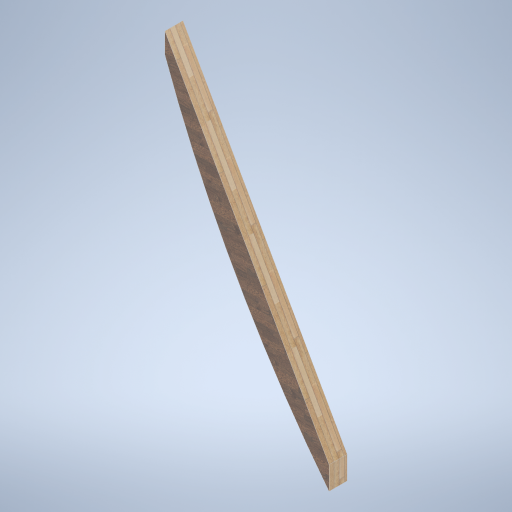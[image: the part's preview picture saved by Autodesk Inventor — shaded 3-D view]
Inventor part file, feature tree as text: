
AUTODESK INVENTOR PART (.ipt)
format: ipt  version: 2024.2 (Build 282272000, 272)  size: 295,424 bytes
history: native  units: in
note: dims shown in document units (in); Inventor stores cm internally (conversion verified against a paired STEP export)
features: other x3, sketch x1
ambient origin geometry x8: Origin, YZ Plane, XZ Plane, XY Plane, X Axis, Y Axis, Z Axis, Center Point
bodies: Body1 (feature_tree)
feature tree (4):
  other  "side_curve_beam_04.ipt"
  other  "Solid2::side_curve_beam_04.ipt"
  other  "TaggingFeature1"
  sketch  "Sketch1"  dims[d0=0.3937in]
